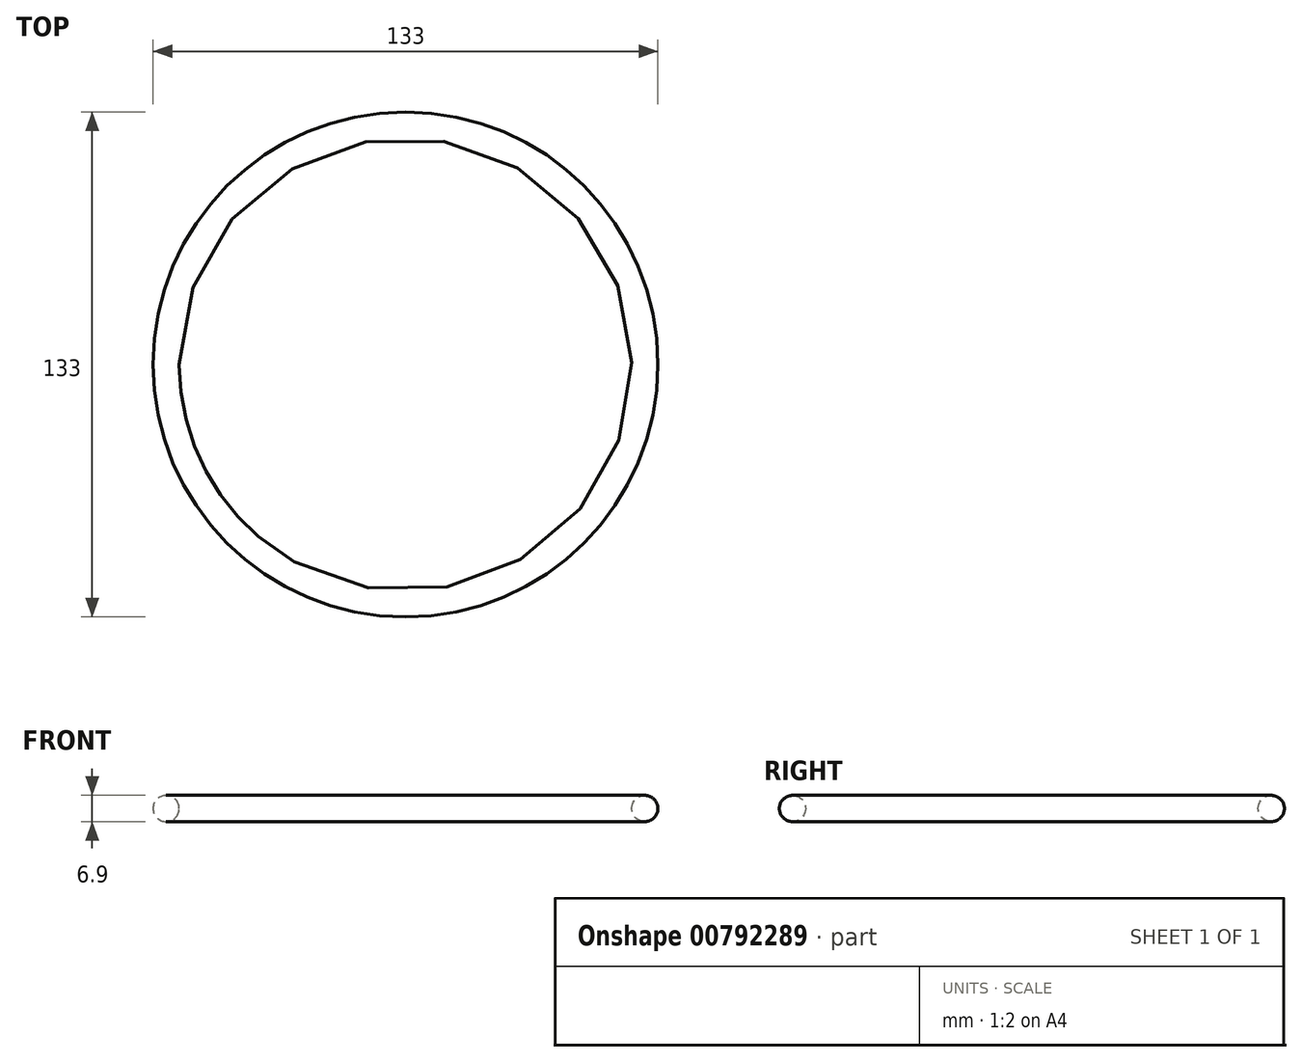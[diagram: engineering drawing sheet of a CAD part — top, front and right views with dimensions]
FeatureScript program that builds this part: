
annotation { "Feature Type Name" : "Feature", "Feature Type Description" : "" }
export const myFeature = defineFeature(function(context is Context, id is Id, definition is map)
    precondition{}
    {
        {
            var Q0;
            Q0=qCreatedBy(makeId("Front.planeOp"),FACE);
            var sketch = newSketch(context, id + "F0", { "sketchPlane" : qUnion([Q0])});
            skCircle(sketch, "E0", {"center": v(63.05, 0) * mm, "radius": 3.45 * mm});
            skLineSegment(sketch, "E1", {"start": v(0, 26.22) * mm, "end": v(0, -13.7) * mm});
            skSolve(sketch);
        }
        {
            var Q0;
            Q0=sQuery(id+"F0.wireOp",EDGE,"E0");
            var Q1;
            Q1=sQuery(id+"F0.wireOp",EDGE,"E1");
            revolve(context, id + "F1", {"bodyType" : ToolBodyType.SURFACE, "surfaceOperationType" : NewSurfaceOperationType.NEW, "surfaceEntities" : qUnion([Q0]), "axis" : qUnion([Q1]), "revolveType" : RevolveType.FULL});
        }
    });
